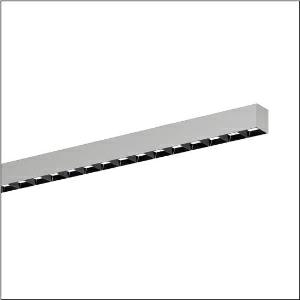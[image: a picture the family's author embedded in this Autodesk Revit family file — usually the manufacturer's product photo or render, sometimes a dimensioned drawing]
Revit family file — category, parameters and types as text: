
# Revit family: silica_r__21_51mx21dc3asb_b009
name_source: partatom
category: Lighting Fixtures
units: mm (PartAtom-declared; Revit-internal decimal feet)

## family parameters
Cut with Voids When Loaded = No
Host = Face
Light Source = No
Part Type = Normal
Room Calculation Point = No
Round Connector Dimension = Use Diameter
Shared = No

## types (1)
- --- (1 x LED, 10800 lm, 69.3 W, 3000K)
    Apparent Load = 69 VA
    CIE Flux Codes = 87 99 100 100 100
    Color Rendering = 80
    Color Temperature = 3000K
    Default Elevation = 1800 mm
    Description = Silica® 21, office luminaire, primary light control with darklight reflector, of PMMA, black, CAT 2 (L<= 3000cd/m²), light emission: direct distribution, primary light characteristic: symmetric, installation type: surface-mounted, LED, rated luminous flux: 10.800lm, luminous efficacy: 156lm/W, light colour: 830, colour temperature: 3000K, with terminal, 3+2-pole, max. 2.5mm², mains connection: 220..240V, AC, 50/60Hz, luminaire housing, of aluminium, metallic grey (RAL 9006), length: 3.004mm, width: 53mm, height: 53mm, protection rating (complete): IP20, insulation class (complete): insulation class I (protective earthing), certification: CE, permissible operating ambient temperature: 0..+35°C, standard: EN 50419, packaging unit: 1 piece
    Height = 0 mm  [stored 0 ft]
    Lamp = 1 x LED
    Lamp Light Flux = 10800 lm
    Lamp Power = 69.3 W
    Lamp count = 1
    Length = 3004 mm
    Luminous efficacy = 156 lm/W
    Manufacturer = Siteco
    ModVariant = No
    Model = 51MX21DC3ASB
    Mounting Place = Ceiling
    Mounting Type = Recessed
    Number of Poles = 1
    OnlyDefault = Yes
    Power Factor = 1
    Product Name = Silica® 21
    Product group = office luminaire | ceiling recessed
    ProductGroupID = 401
    Protection Class = Protection class I
    Protection Degree = IP 20
    RLX_Detail_Level = 1
    RLX_Emergency_Light_Flux = 0 lm
    RLX_Emergency_Type = 0
    RLX_Emergency_Type_DB = No
    RlxData = <blob elided: 64533 chars, md5=56e5dd15>
    Socket = socket
    Standby Power = 0 W
    System Light Flux = 10800 lm
    System Power = 69 W
    Type Comments = factory setting: luminous flux: 100 % | dim-lin: 254 | 393 mA
    Type Image = l_1297764.jpg
    URL = http://relux.com
    VarID = @adj_054275
    Voltage = 0 V
    Weight = 0.00 kg
    Width = 53 mm

note: [stored X ft] marks values corroborated as IEEE doubles in the binary element streams (Revit-internal decimal feet)

## geometry (parser evidence)
native form markers: Blend x4, Sweep x12
no freeform markers — native parametric forms only
